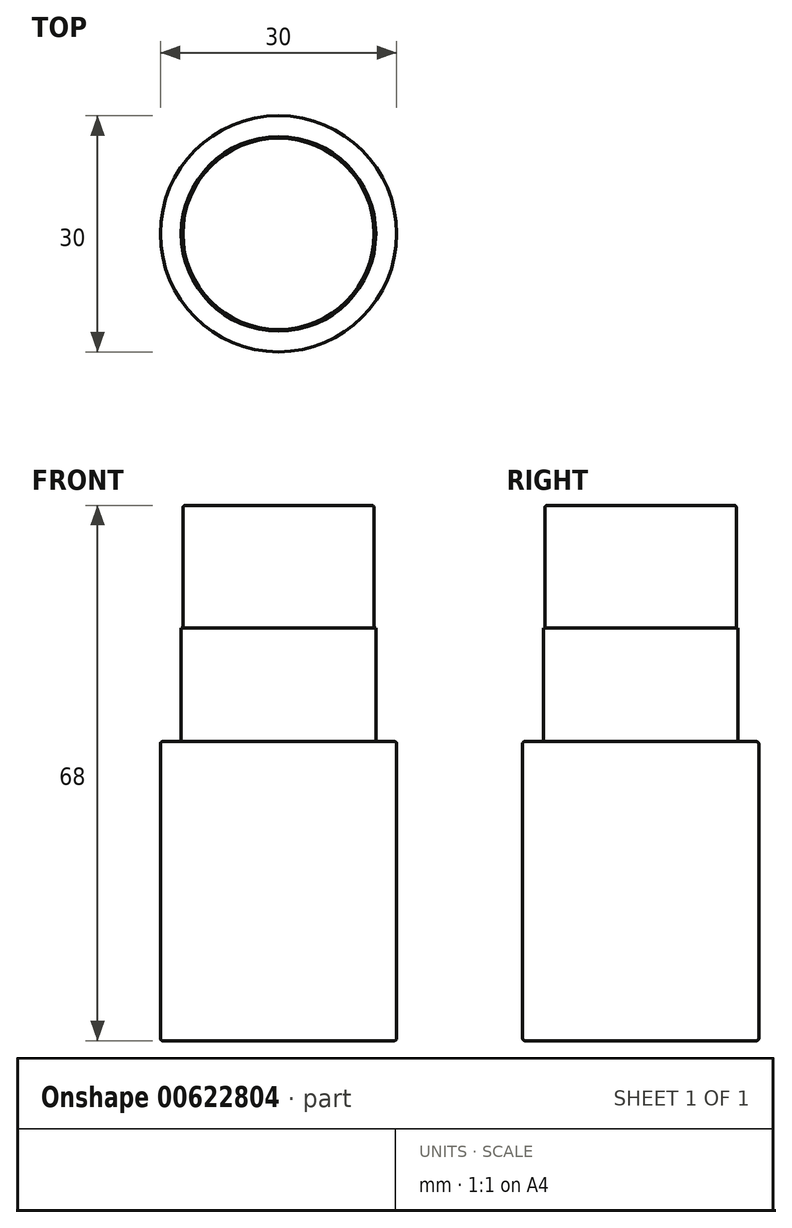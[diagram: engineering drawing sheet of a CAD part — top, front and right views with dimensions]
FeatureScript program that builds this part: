
annotation { "Feature Type Name" : "Feature", "Feature Type Description" : "" }
export const myFeature = defineFeature(function(context is Context, id is Id, definition is map)
    precondition{}
    {
        {
            var Q0;
            Q0=qCreatedBy(makeId("Front.planeOp"),FACE);
            var sketch = newSketch(context, id + "F0", { "sketchPlane" : qUnion([Q0])});
            skLineSegment(sketch, "E0", {"start": v(0, 30) * mm, "end": v(12.15, 30) * mm});
            skLineSegment(sketch, "E1", {"start": v(12.15, 30) * mm, "end": v(12.15, 14.45) * mm});
            skLineSegment(sketch, "E2", {"start": v(12.15, 14.45) * mm, "end": v(12.36, 14.45) * mm});
            skLineSegment(sketch, "E3", {"start": v(12.36, 14.45) * mm, "end": v(12.36, 0) * mm});
            skLineSegment(sketch, "E4", {"start": v(12.36, 0) * mm, "end": v(15, 0) * mm});
            skLineSegment(sketch, "E5", {"start": v(15, 0) * mm, "end": v(15, -38) * mm});
            skLineSegment(sketch, "E6", {"start": v(15, -38) * mm, "end": v(0, -38) * mm});
            skLineSegment(sketch, "E7", {"start": v(0, -38) * mm, "end": v(0, 30) * mm, "construction": true});
            skLineSegment(sketch, "E8", {"start": v(0, 30) * mm, "end": v(0, -38) * mm});
            skSolve(sketch);
        }
        {
            var Q0;
            Q0=makeQuery(id+"F0.imprint","IMPRINT",FACE,{"disambiguationData":[TD([[makeQuery(id+"F0.imprint","IMPRINT",EDGE,{"derivedFrom":sQuery(id+"F0.wireOp",EDGE,"E0")}),-1.0]])]});
            var Q1;
            Q1=sQuery(id+"F0.wireOp",EDGE,"E8");
            revolve(context, id + "F1", {"entities" : qUnion([Q0]), "axis" : qUnion([Q1]), "revolveType" : RevolveType.FULL});
        }
        {
            var Q0;
            Q0=makeQuery(id+"F1.opRevolve","SWEPT_EDGE",EDGE,{"disambiguationData":[OSD([sQuery(id+"F0.wireOp",EDGE,"E0"),sQuery(id+"F0.wireOp",EDGE,"E1")])]});
            var Q1;
            Q1=makeQuery(id+"F1.opRevolve","SWEPT_EDGE",EDGE,{"disambiguationData":[OSD([sQuery(id+"F0.wireOp",EDGE,"E4"),sQuery(id+"F0.wireOp",EDGE,"E5")])]});
            var Q2;
            Q2=makeQuery(id+"F1.opRevolve","SWEPT_EDGE",EDGE,{"disambiguationData":[OSD([sQuery(id+"F0.wireOp",EDGE,"E5"),sQuery(id+"F0.wireOp",EDGE,"E6")])]});
            fillet(context, id + "F2", {"entities" : qUnion([Q0, Q1, Q2]), "radius" : 0.3 * mm, "tangentPropagation" : true, "allowEdgeOverflow" : false});
        }
    });
